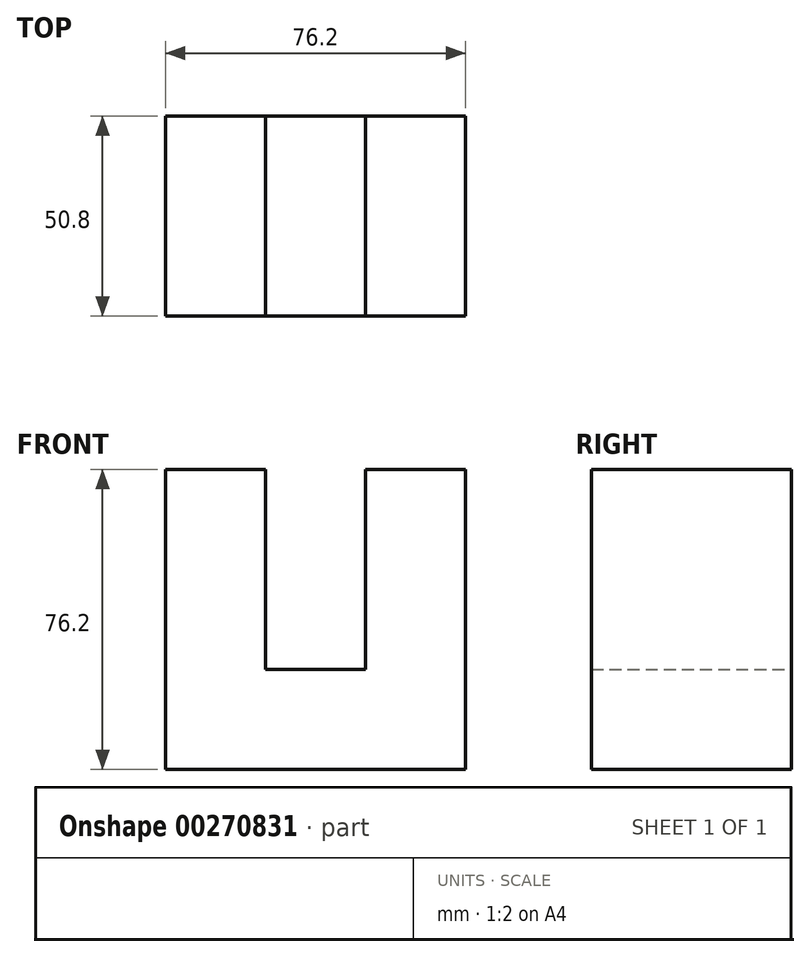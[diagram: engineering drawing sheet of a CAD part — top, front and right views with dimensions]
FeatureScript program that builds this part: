
annotation { "Feature Type Name" : "Feature", "Feature Type Description" : "" }
export const myFeature = defineFeature(function(context is Context, id is Id, definition is map)
    precondition{}
    {
        {
            var Q0;
            Q0=qCreatedBy(makeId("Front.planeOp"),FACE);
            var sketch = newSketch(context, id + "F0", { "sketchPlane" : qUnion([Q0])});
            skLineSegment(sketch, "E0", {"start": v(0, 0) * mm, "end": v(0, 76.2) * mm});
            skLineSegment(sketch, "E1", {"start": v(0, 0) * mm, "end": v(-76.2, 0) * mm});
            skLineSegment(sketch, "E2", {"start": v(-76.2, 0) * mm, "end": v(-76.2, 76.2) * mm});
            skLineSegment(sketch, "E3", {"start": v(-76.2, 76.2) * mm, "end": v(-50.8, 76.2) * mm});
            skLineSegment(sketch, "E4", {"start": v(0, 76.2) * mm, "end": v(-25.4, 76.2) * mm});
            skLineSegment(sketch, "E5", {"start": v(-25.4, 76.2) * mm, "end": v(-25.4, 25.4) * mm});
            skLineSegment(sketch, "E6", {"start": v(-50.8, 76.2) * mm, "end": v(-50.8, 25.4) * mm});
            skLineSegment(sketch, "E7", {"start": v(-25.4, 25.4) * mm, "end": v(-50.8, 25.4) * mm});
            skSolve(sketch);
        }
        {
            var Q0;
            Q0 = qSketchRegion(id + "F0", true);
            extrude(context, id + "F1", {"entities" : qUnion([Q0]), "depth" : 50.8 * mm});
        }
    });
